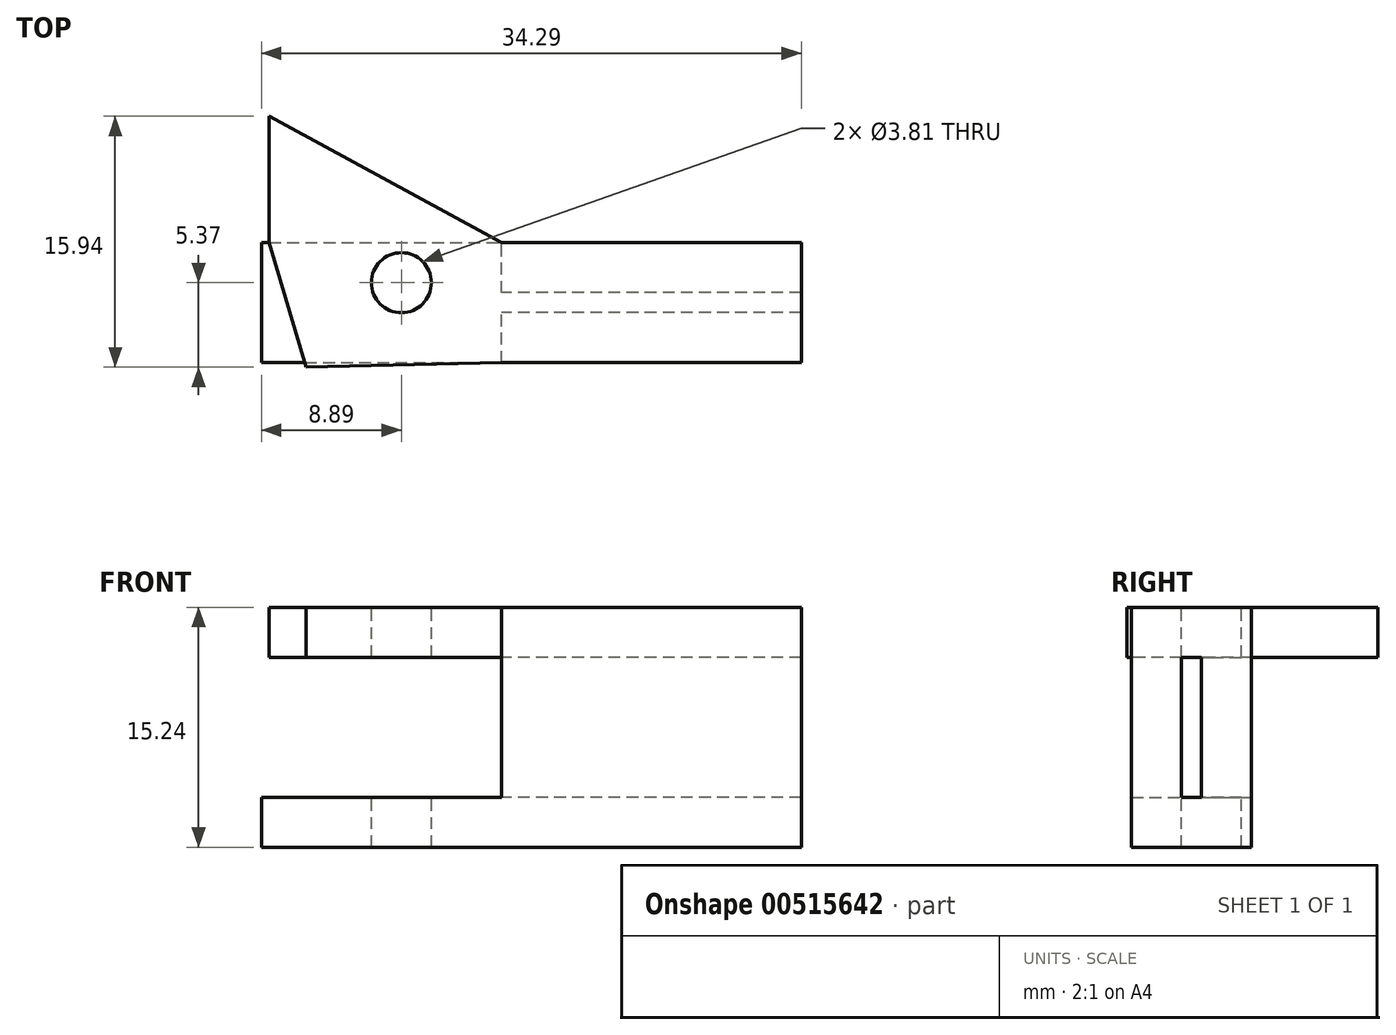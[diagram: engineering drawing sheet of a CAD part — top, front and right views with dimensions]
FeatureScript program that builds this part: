
annotation { "Feature Type Name" : "Feature", "Feature Type Description" : "" }
export const myFeature = defineFeature(function(context is Context, id is Id, definition is map)
    precondition{}
    {
        {
            var Q0;
            Q0=qCreatedBy(makeId("Right.planeOp"),FACE);
            var sketch = newSketch(context, id + "F0", { "sketchPlane" : qUnion([Q0])});
            skLineSegment(sketch, "E0.bottom", {"start": v(0, 0) * mm, "end": v(-7.62, 0) * mm});
            skLineSegment(sketch, "E0.top", {"start": v(0, 15.24) * mm, "end": v(-7.62, 15.24) * mm});
            skLineSegment(sketch, "E0.left", {"start": v(0, 0) * mm, "end": v(0, 15.24) * mm});
            skLineSegment(sketch, "E0.right", {"start": v(-7.62, 0) * mm, "end": v(-7.62, 15.24) * mm});
            skSolve(sketch);
        }
        {
            var Q0;
            Q0 = qSketchRegion(id + "F0", true);
            extrude(context, id + "F1", {"entities" : qUnion([Q0]), "depth" : 19.05 * mm, "offsetDistance" : 25.4 * mm});
        }
        {
            var Q0;
            Q0=makeQuery(id+"F1.opExtrude","CAP_FACE",FACE,{"disambiguationData":[OSD([sQuery(id+"F0.wireOp",EDGE,"E0.bottom"),sQuery(id+"F0.wireOp",EDGE,"E0.top"),sQuery(id+"F0.wireOp",EDGE,"E0.left"),sQuery(id+"F0.wireOp",EDGE,"E0.right")])],"isStart":true});
            var Q1;
            Q1=makeQuery(id+"F1.opExtrude","CAP_FACE",FACE,{"disambiguationData":[OSD([sQuery(id+"F0.wireOp",EDGE,"E0.bottom"),sQuery(id+"F0.wireOp",EDGE,"E0.top"),sQuery(id+"F0.wireOp",EDGE,"E0.left"),sQuery(id+"F0.wireOp",EDGE,"E0.right")])],"isStart":false});
            var Q2;
            Q2=makeQuery(id+"F1.opExtrude","SWEPT_BODY",BODY,{"disambiguationData":[OSD([sQuery(id+"F0.wireOp",EDGE,"E0.bottom"),sQuery(id+"F0.wireOp",EDGE,"E0.top"),sQuery(id+"F0.wireOp",EDGE,"E0.left"),sQuery(id+"F0.wireOp",EDGE,"E0.right")])]});
            shell(context, id + "F2", {"entities" : qUnion([Q0, Q1]), "parts" : qUnion([Q2]), "thickness" : 3.17 * mm});
        }
        {
            var Q0;
            Q0=makeQuery(id+"F1.opExtrude","SWEPT_FACE",FACE,{"disambiguationData":[OSD([sQuery(id+"F0.wireOp",EDGE,"E0.top")])]});
            var sketch = newSketch(context, id + "F3", { "sketchPlane" : qUnion([Q0])});
            skLineSegment(sketch, "E1", {"start": v(0, -7.62) * mm, "end": v(-12.4, -7.9) * mm});
            skLineSegment(sketch, "E2", {"start": v(-12.4, -7.9) * mm, "end": v(-14.74, 0) * mm});
            skLineSegment(sketch, "E3", {"start": v(-14.74, 0) * mm, "end": v(-14.74, 8.03) * mm});
            skLineSegment(sketch, "E4", {"start": v(-14.74, 8.03) * mm, "end": v(0, 0) * mm});
            skSolve(sketch);
        }
        {
            var Q0;
            Q0 = qSketchRegion(id + "F3", true);
            var Q1;
            Q1=makeQuery(id+"F3.imprint","IMPRINT",FACE,{"disambiguationData":[TD([[makeQuery(id+"F3.imprint","IMPRINT",EDGE,{"derivedFrom":sQuery(id+"F3.wireOp",EDGE,"E1")}),-1.0]])]});
            var Q2;
            Q2=makeQuery(id+"F2.opShell","OFFSET_FACE",FACE,{"disambiguationData":[OSD([sQuery(id+"F0.wireOp",EDGE,"E0.top")])]});
            extrude(context, id + "F4", {"entities" : qUnion([Q0, Q1]), "operationType" : NewBodyOperationType.ADD, "endBound" : BoundingType.UP_TO_SURFACE, "oppositeDirection" : true, "depth" : 3.17 * mm, "endBoundEntityFace" : qUnion([Q2]), "offsetDistance" : 25.4 * mm});
        }
        {
            var Q0;
            Q0=makeQuery(id+"F1.opExtrude","SWEPT_FACE",FACE,{"disambiguationData":[OSD([sQuery(id+"F0.wireOp",EDGE,"E0.bottom")])]});
            var sketch = newSketch(context, id + "F5", { "sketchPlane" : qUnion([Q0])});
            skLineSegment(sketch, "E5.bottom", {"start": v(0, 7.62) * mm, "end": v(-15.24, 7.62) * mm});
            skLineSegment(sketch, "E5.top", {"start": v(0, 0) * mm, "end": v(-15.24, 0) * mm});
            skLineSegment(sketch, "E5.left", {"start": v(0, 7.62) * mm, "end": v(0, 0) * mm});
            skLineSegment(sketch, "E5.right", {"start": v(-15.24, 7.62) * mm, "end": v(-15.24, 0) * mm});
            skSolve(sketch);
        }
        {
            var Q0;
            Q0 = qSketchRegion(id + "F5", true);
            var Q1;
            Q1=makeQuery(id+"F2.opShell","OFFSET_FACE",FACE,{"disambiguationData":[OSD([sQuery(id+"F0.wireOp",EDGE,"E0.bottom")])]});
            extrude(context, id + "F6", {"entities" : qUnion([Q0]), "operationType" : NewBodyOperationType.ADD, "endBound" : BoundingType.UP_TO_SURFACE, "oppositeDirection" : true, "depth" : 25.4 * mm, "endBoundEntityFace" : qUnion([Q1]), "offsetDistance" : 25.4 * mm});
        }
        {
            var Q0;
            {var subQ0=sQuery(id+"F0.wireOp",EDGE,"E0.top");Q0=makeQuery(id+"F4.boolean.opBoolean","MERGE",FACE,{"derivedFrom":[makeQuery(id+"F1.opExtrude","SWEPT_FACE",FACE,{"disambiguationData":[OSD([subQ0])]}),makeQuery(id+"F4.opExtrude","CAP_FACE",FACE,{"disambiguationData":[OSD([subQ0,sQuery(id+"F3.wireOp",EDGE,"E1"),sQuery(id+"F3.wireOp",EDGE,"E2"),sQuery(id+"F3.wireOp",EDGE,"E3"),sQuery(id+"F3.wireOp",EDGE,"E4")])],"isStart":true})]});}
            var sketch = newSketch(context, id + "F7", { "sketchPlane" : qUnion([Q0])});
            skCircle(sketch, "E6", {"center": v(-6.35, -2.54) * mm, "radius": 1.9 * mm});
            skSolve(sketch);
        }
        {
            var Q0;
            Q0 = qSketchRegion(id + "F7", true);
            extrude(context, id + "F8", {"entities" : qUnion([Q0]), "operationType" : NewBodyOperationType.REMOVE, "endBound" : BoundingType.THROUGH_ALL, "oppositeDirection" : true, "depth" : 25.4 * mm, "offsetDistance" : 25.4 * mm});
        }
    });
